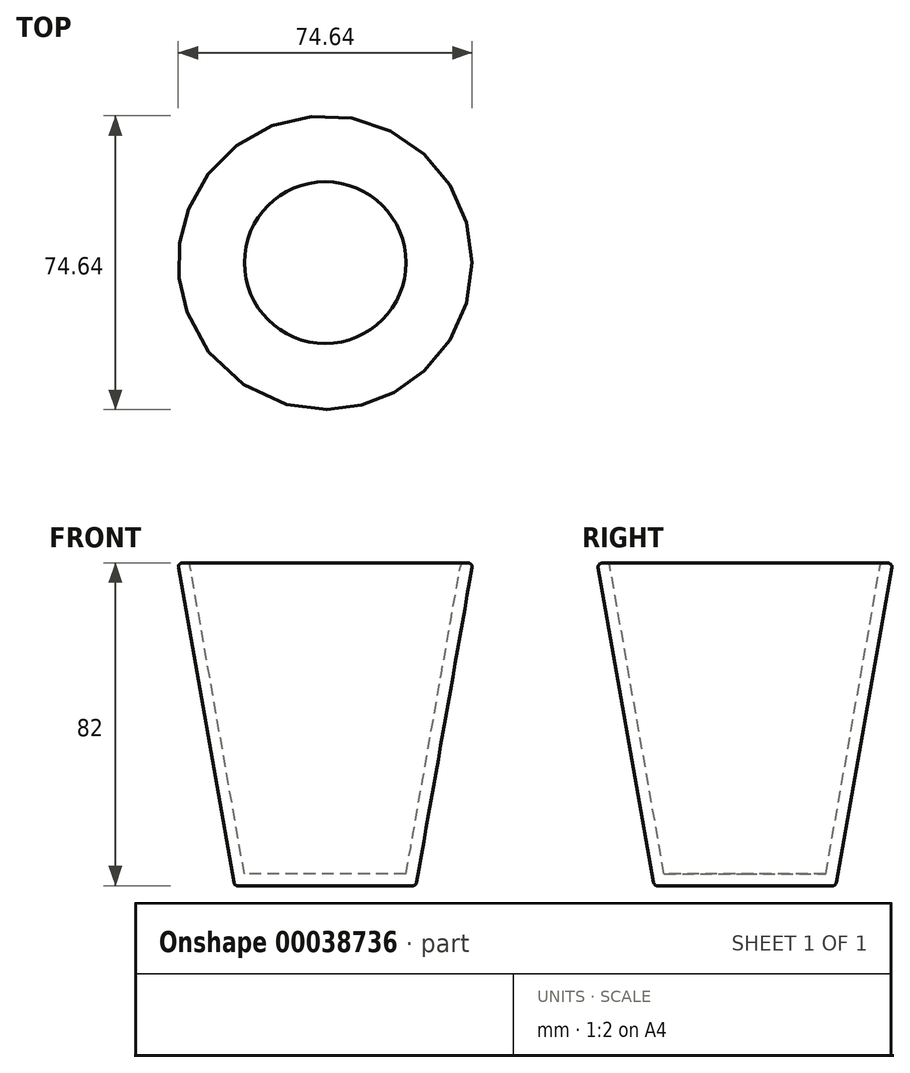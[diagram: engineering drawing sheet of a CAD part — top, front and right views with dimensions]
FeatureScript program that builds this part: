
annotation { "Feature Type Name" : "Feature", "Feature Type Description" : "" }
export const myFeature = defineFeature(function(context is Context, id is Id, definition is map)
    precondition{}
    {
        {
            var Q0;
            Q0=qCreatedBy(makeId("Top.planeOp"),FACE);
            var sketch = newSketch(context, id + "F0", { "sketchPlane" : qUnion([Q0])});
            skCircle(sketch, "E0", {"center": v(0, 0) * mm, "radius": 23.05 * mm});
            skSolve(sketch);
        }
        {
            var Q0;
            Q0=makeQuery(id+"F0.imprint","IMPRINT",FACE,{"disambiguationData":[TD([[makeQuery(id+"F0.imprint","IMPRINT",EDGE,{"derivedFrom":sQuery(id+"F0.wireOp",EDGE,"E0")}),1.0]])]});
            extrude(context, id + "F1", {"entities" : qUnion([Q0]), "depth" : 82 * mm, "hasDraft" : true, "draftAngle" : 10 * degree});
        }
        {
            var Q0;
            Q0=makeQuery(id+"F1.opExtrude","CAP_FACE",FACE,{"disambiguationData":[OSD([sQuery(id+"F0.wireOp",EDGE,"E0")])],"isStart":false});
            shell(context, id + "F2", {"entities" : qUnion([Q0]), "thickness" : 3 * mm});
        }
        {
            var Q0;
            Q0=makeQuery(id+"F1.opExtrude","CAP_EDGE",EDGE,{"disambiguationData":[OSD([sQuery(id+"F0.wireOp",EDGE,"E0")])],"isStart":false});
            var Q1;
            {var subQ0=sQuery(id+"F0.wireOp",EDGE,"E0");Q1=makeQuery(id+"F2.opShell","OFFSET_EDGE",EDGE,{"disambiguationData":[OSD([subQ0]),TDD([makeQuery(id+"F1.opExtrude","CAP_EDGE",EDGE,{"disambiguationData":[OSD([subQ0])],"isStart":false})])]});}
            var Q2;
            Q2=makeQuery(id+"F1.opExtrude","CAP_EDGE",EDGE,{"disambiguationData":[OSD([sQuery(id+"F0.wireOp",EDGE,"E0")])],"isStart":true});
            fillet(context, id + "F3", {"entities" : qUnion([Q0, Q1, Q2]), "radius" : 1 * mm, "tangentPropagation" : true, "allowEdgeOverflow" : false});
        }
    });
